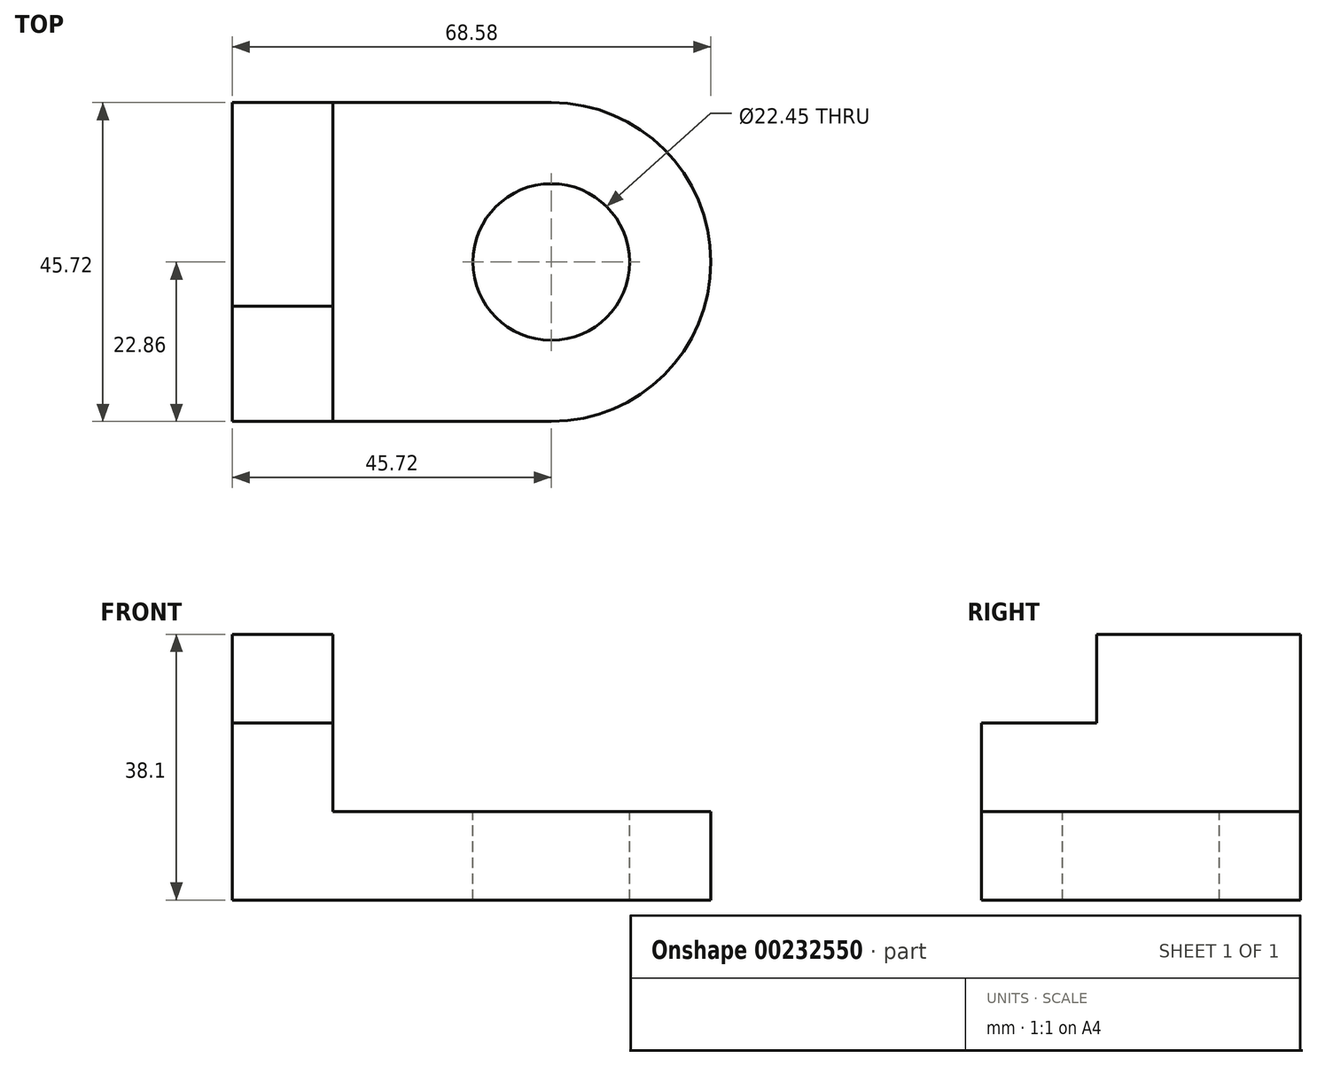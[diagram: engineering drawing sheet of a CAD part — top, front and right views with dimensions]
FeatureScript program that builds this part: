
annotation { "Feature Type Name" : "Feature", "Feature Type Description" : "" }
export const myFeature = defineFeature(function(context is Context, id is Id, definition is map)
    precondition{}
    {
        {
            var Q0;
            Q0=qCreatedBy(makeId("Top.planeOp"),FACE);
            var sketch = newSketch(context, id + "F0", { "sketchPlane" : qUnion([Q0])});
            skLineSegment(sketch, "E0.bottom", {"start": v(22.86, -22.86) * mm, "end": v(-22.86, -22.86) * mm});
            skLineSegment(sketch, "E0.top", {"start": v(22.86, 22.86) * mm, "end": v(-22.86, 22.86) * mm});
            skLineSegment(sketch, "E0.right", {"start": v(-22.86, -22.86) * mm, "end": v(-22.86, 22.86) * mm});
            skPoint(sketch, "E0.middle", {"position": v(0, 0) * mm});
            skArc(sketch, "E1", {"start": v(22.86, -22.86) * mm, "mid": v(45.72, 0) * mm, "end": v(22.86, 22.86) * mm});
            skSolve(sketch);
        }
        {
            var Q0;
            Q0=makeQuery(id+"F0.imprint","IMPRINT",FACE,{"disambiguationData":[TD([[makeQuery(id+"F0.imprint","IMPRINT",EDGE,{"derivedFrom":sQuery(id+"F0.wireOp",EDGE,"E0.bottom")}),-1.0]])]});
            extrude(context, id + "F1", {"entities" : qUnion([Q0]), "depth" : 12.7 * mm});
        }
        {
            var Q0;
            Q0=makeQuery(id+"F1.opExtrude","CAP_FACE",FACE,{"disambiguationData":[OSD([sQuery(id+"F0.wireOp",EDGE,"E0.bottom"),sQuery(id+"F0.wireOp",EDGE,"E0.top"),sQuery(id+"F0.wireOp",EDGE,"E0.right"),sQuery(id+"F0.wireOp",EDGE,"E1")])],"isStart":false});
            var sketch = newSketch(context, id + "F2", { "sketchPlane" : qUnion([Q0])});
            skLineSegment(sketch, "E2.bottom", {"start": v(-22.86, 22.86) * mm, "end": v(-8.46, 22.86) * mm});
            skLineSegment(sketch, "E2.top", {"start": v(-22.86, -22.86) * mm, "end": v(-8.46, -22.86) * mm});
            skLineSegment(sketch, "E2.left", {"start": v(-22.86, 22.86) * mm, "end": v(-22.86, -22.86) * mm});
            skLineSegment(sketch, "E2.right", {"start": v(-8.46, 22.86) * mm, "end": v(-8.46, -22.86) * mm});
            skSolve(sketch);
        }
        {
            var Q0;
            Q0=makeQuery(id+"F2.imprint","IMPRINT",FACE,{"disambiguationData":[TD([[makeQuery(id+"F2.imprint","IMPRINT",EDGE,{"derivedFrom":sQuery(id+"F2.wireOp",EDGE,"E2.bottom")}),1.0]])]});
            extrude(context, id + "F3", {"entities" : qUnion([Q0]), "operationType" : NewBodyOperationType.ADD, "depth" : 12.7 * mm});
        }
        {
            var Q0;
            Q0=makeQuery(id+"F3.opExtrude","CAP_FACE",FACE,{"disambiguationData":[OSD([sQuery(id+"F2.wireOp",EDGE,"E2.bottom"),sQuery(id+"F2.wireOp",EDGE,"E2.top"),sQuery(id+"F2.wireOp",EDGE,"E2.left"),sQuery(id+"F2.wireOp",EDGE,"E2.right")])],"isStart":false});
            var sketch = newSketch(context, id + "F4", { "sketchPlane" : qUnion([Q0])});
            skLineSegment(sketch, "E3.bottom", {"start": v(-22.86, 22.86) * mm, "end": v(-8.46, 22.86) * mm});
            skLineSegment(sketch, "E3.top", {"start": v(-22.86, -6.33) * mm, "end": v(-8.46, -6.33) * mm});
            skLineSegment(sketch, "E3.left", {"start": v(-22.86, 22.86) * mm, "end": v(-22.86, -6.33) * mm});
            skLineSegment(sketch, "E3.right", {"start": v(-8.46, 22.86) * mm, "end": v(-8.46, -6.33) * mm});
            skSolve(sketch);
        }
        {
            var Q0;
            Q0=makeQuery(id+"F4.imprint","IMPRINT",FACE,{"disambiguationData":[TD([[makeQuery(id+"F4.imprint","IMPRINT",EDGE,{"derivedFrom":sQuery(id+"F4.wireOp",EDGE,"E3.bottom")}),1.0]])]});
            extrude(context, id + "F5", {"entities" : qUnion([Q0]), "operationType" : NewBodyOperationType.ADD, "depth" : 12.7 * mm});
        }
        {
            var Q0;
            Q0=makeQuery(id+"F1.opExtrude","CAP_FACE",FACE,{"disambiguationData":[OSD([sQuery(id+"F0.wireOp",EDGE,"E0.bottom"),sQuery(id+"F0.wireOp",EDGE,"E0.top"),sQuery(id+"F0.wireOp",EDGE,"E0.right"),sQuery(id+"F0.wireOp",EDGE,"E1")])],"isStart":false});
            var sketch = newSketch(context, id + "F6", { "sketchPlane" : qUnion([Q0])});
            skCircle(sketch, "E4", {"center": v(22.86, 0) * mm, "radius": 11.23 * mm});
            skSolve(sketch);
        }
        {
            var Q0;
            Q0=makeQuery(id+"F6.imprint","IMPRINT",FACE,{"disambiguationData":[TD([[makeQuery(id+"F6.imprint","IMPRINT",EDGE,{"derivedFrom":sQuery(id+"F6.wireOp",EDGE,"E4")}),1.0]])]});
            extrude(context, id + "F7", {"entities" : qUnion([Q0]), "operationType" : NewBodyOperationType.REMOVE, "oppositeDirection" : true, "depth" : 25.4 * mm});
        }
    });
